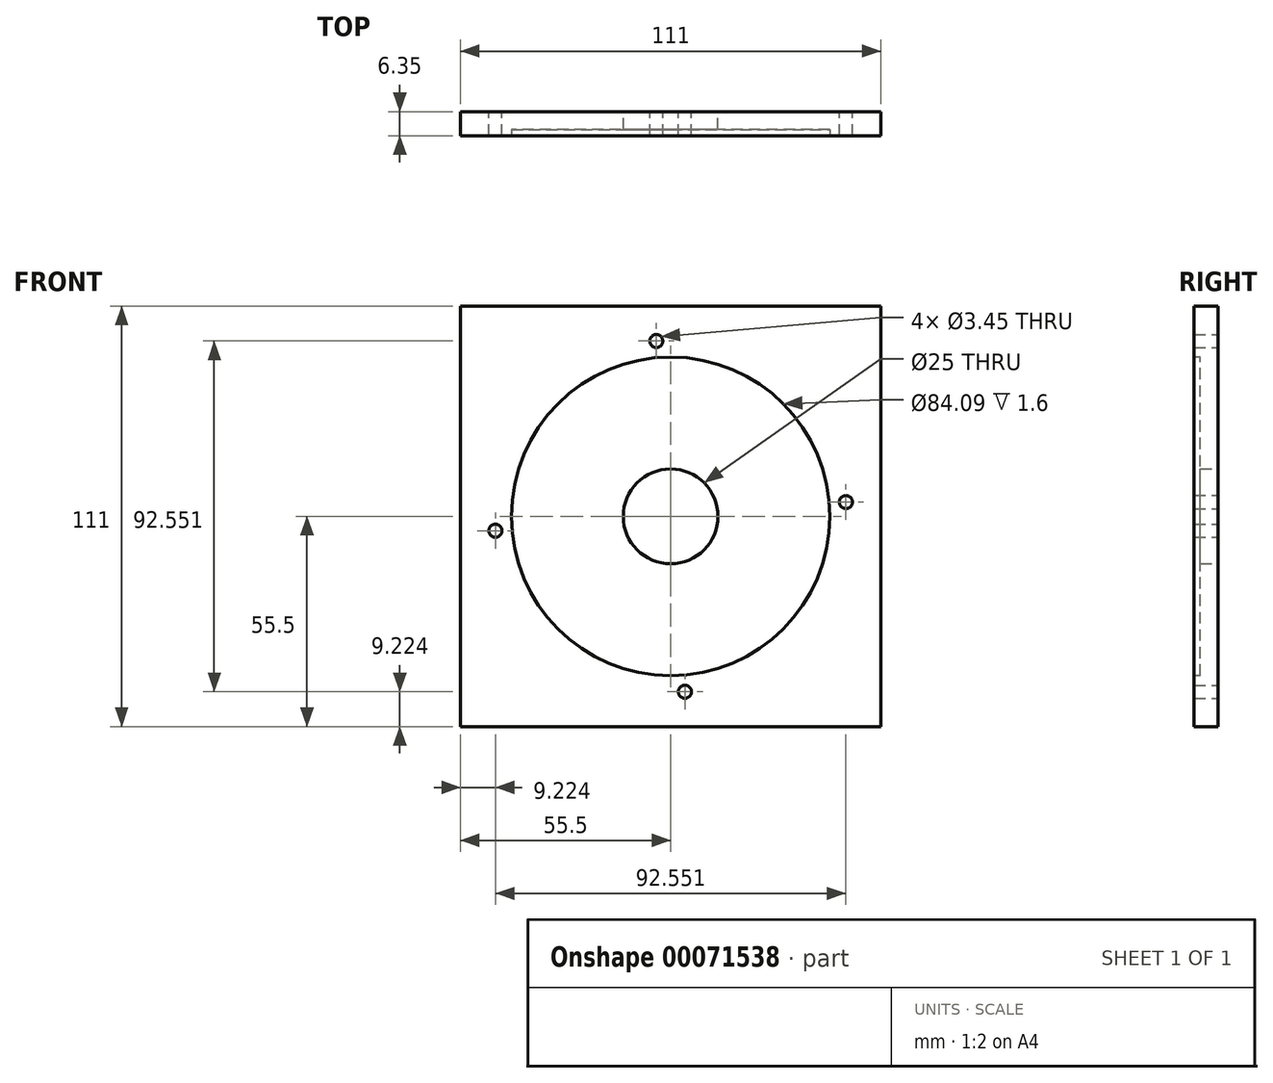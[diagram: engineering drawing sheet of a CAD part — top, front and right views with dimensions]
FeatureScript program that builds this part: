
annotation { "Feature Type Name" : "Feature", "Feature Type Description" : "" }
export const myFeature = defineFeature(function(context is Context, id is Id, definition is map)
    precondition{}
    {
        {
            var Q0;
            Q0=qCreatedBy(makeId("Front.planeOp"),FACE);
            var sketch = newSketch(context, id + "F0", { "sketchPlane" : qUnion([Q0])});
            skCircle(sketch, "E0", {"center": v(0, 0) * mm, "radius": 12.5 * mm});
            skCircle(sketch, "E1", {"center": v(-46.28, -3.78) * mm, "radius": 1.73 * mm});
            skCircle(sketch, "E2.1.0", {"center": v(3.78, -46.28) * mm, "radius": 1.73 * mm});
            skCircle(sketch, "E2.2.0", {"center": v(46.28, 3.78) * mm, "radius": 1.73 * mm});
            skCircle(sketch, "E2.3.0", {"center": v(-3.78, 46.28) * mm, "radius": 1.73 * mm});
            skLineSegment(sketch, "E3.bottom", {"start": v(-55.5, 55.5) * mm, "end": v(55.5, 55.5) * mm});
            skLineSegment(sketch, "E3.top", {"start": v(-55.5, -55.5) * mm, "end": v(55.5, -55.5) * mm});
            skLineSegment(sketch, "E3.left", {"start": v(-55.5, 55.5) * mm, "end": v(-55.5, -55.5) * mm});
            skLineSegment(sketch, "E3.right", {"start": v(55.5, 55.5) * mm, "end": v(55.5, -55.5) * mm});
            skSolve(sketch);
        }
        {
            var Q0;
            Q0=makeQuery(id+"F0.imprint","IMPRINT",FACE,{"disambiguationData":[TD([[makeQuery(id+"F0.imprint","IMPRINT",EDGE,{"derivedFrom":sQuery(id+"F0.wireOp",EDGE,"AXm76Gkz-KgOu-L99j-iJxS-TcNf85blTNp5")}),1.0]])]});
            var Q1;
            Q1=makeQuery(id+"F0.imprint","IMPRINT",FACE,{"disambiguationData":[TD([[makeQuery(id+"F0.imprint","IMPRINT",EDGE,{"derivedFrom":sQuery(id+"F0.wireOp",EDGE,"E0")}),-1.0]])]});
            extrude(context, id + "F1", {"entities" : qUnion([Q0, Q1]), "depth" : 6.35 * mm});
        }
        {
            var Q0;
            Q0=makeQuery(id+"F1.opExtrude","CAP_FACE",FACE,{"disambiguationData":[OSD([sQuery(id+"F0.wireOp",EDGE,"E0"),sQuery(id+"F0.wireOp",EDGE,"E1"),sQuery(id+"F0.wireOp",EDGE,"E2.1.0"),sQuery(id+"F0.wireOp",EDGE,"E2.2.0"),sQuery(id+"F0.wireOp",EDGE,"E2.3.0"),sQuery(id+"F0.wireOp",EDGE,"E3.bottom"),sQuery(id+"F0.wireOp",EDGE,"E3.top"),sQuery(id+"F0.wireOp",EDGE,"E3.left"),sQuery(id+"F0.wireOp",EDGE,"E3.right")])],"isStart":false});
            var sketch = newSketch(context, id + "F2", { "sketchPlane" : qUnion([Q0])});
            skCircle(sketch, "E4", {"center": v(0, 0) * mm, "radius": 42.05 * mm});
            skSolve(sketch);
        }
        {
            var Q0;
            Q0 = qSketchRegion(id + "F2", true);
            extrude(context, id + "F3", {"entities" : qUnion([Q0]), "operationType" : NewBodyOperationType.REMOVE, "oppositeDirection" : true, "depth" : 1.6 * mm});
        }
    });
